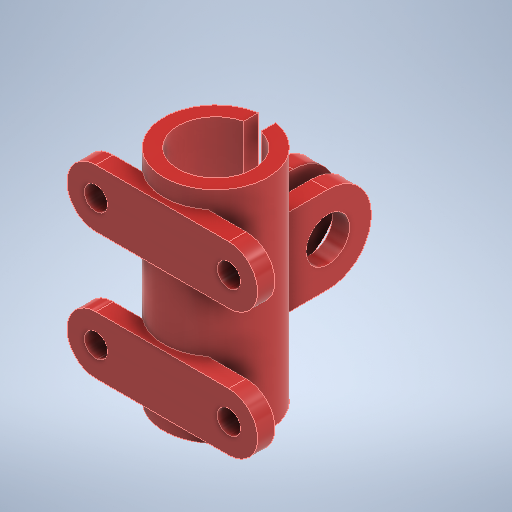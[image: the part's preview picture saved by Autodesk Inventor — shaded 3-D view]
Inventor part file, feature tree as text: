
AUTODESK INVENTOR PART (.ipt)
format: ipt  version: 2025.2 (Build 292293000, 293)  size: 360,448 bytes
history: native  units: in
note: dims shown in document units (in); Inventor stores cm internally (conversion verified against a paired STEP export)
features: sketch x6, extrude x3, plane x2, mirror x1
ambient origin geometry x8: Origin, YZ Plane, XZ Plane, XY Plane, X Axis, Y Axis, Z Axis, Center Point
bodies: Solid1 (feature_tree)
feature tree (12):
  extrude  "Extrusion1"  Depth=0.9843in
  sketch  "Sketch2"  dims[d2=0.7874in d3=0.7874in]
  sketch  "Sketch3"  dims[d4=4.5276in d5=0.9843in d6=0.7874in d7=0.7874in d8=4.3307in d9=0.5906in d10=0.0in]
  extrude  "Extrusion2"  Depth=0.7874in
  sketch  "Sketch5"  dims[d12=3.5433in]
  plane  "Work Plane1"
  extrude  "Extrusion3"  Depth=0.5906in TaperAngle=0.0deg
  plane  "Work Plane2"
  mirror  "Mirror1"
  sketch  "Sketch1"  dims[d0=4.5276in d1=0.9843in]
  sketch  "Sketch4"  dims[d11=6.4961in]
  sketch  "Sketch6"  dims[d13=1.378in d14=2.5591in d15=0.5906in d16=3.5433in d17=0.5906in d18=6.8898in d19=0.0in d20=0.0in d21=1.4764in d22=2.9528in d26=0.5906in d27=0.0in d28=0.0197in d29=0.0344in]
